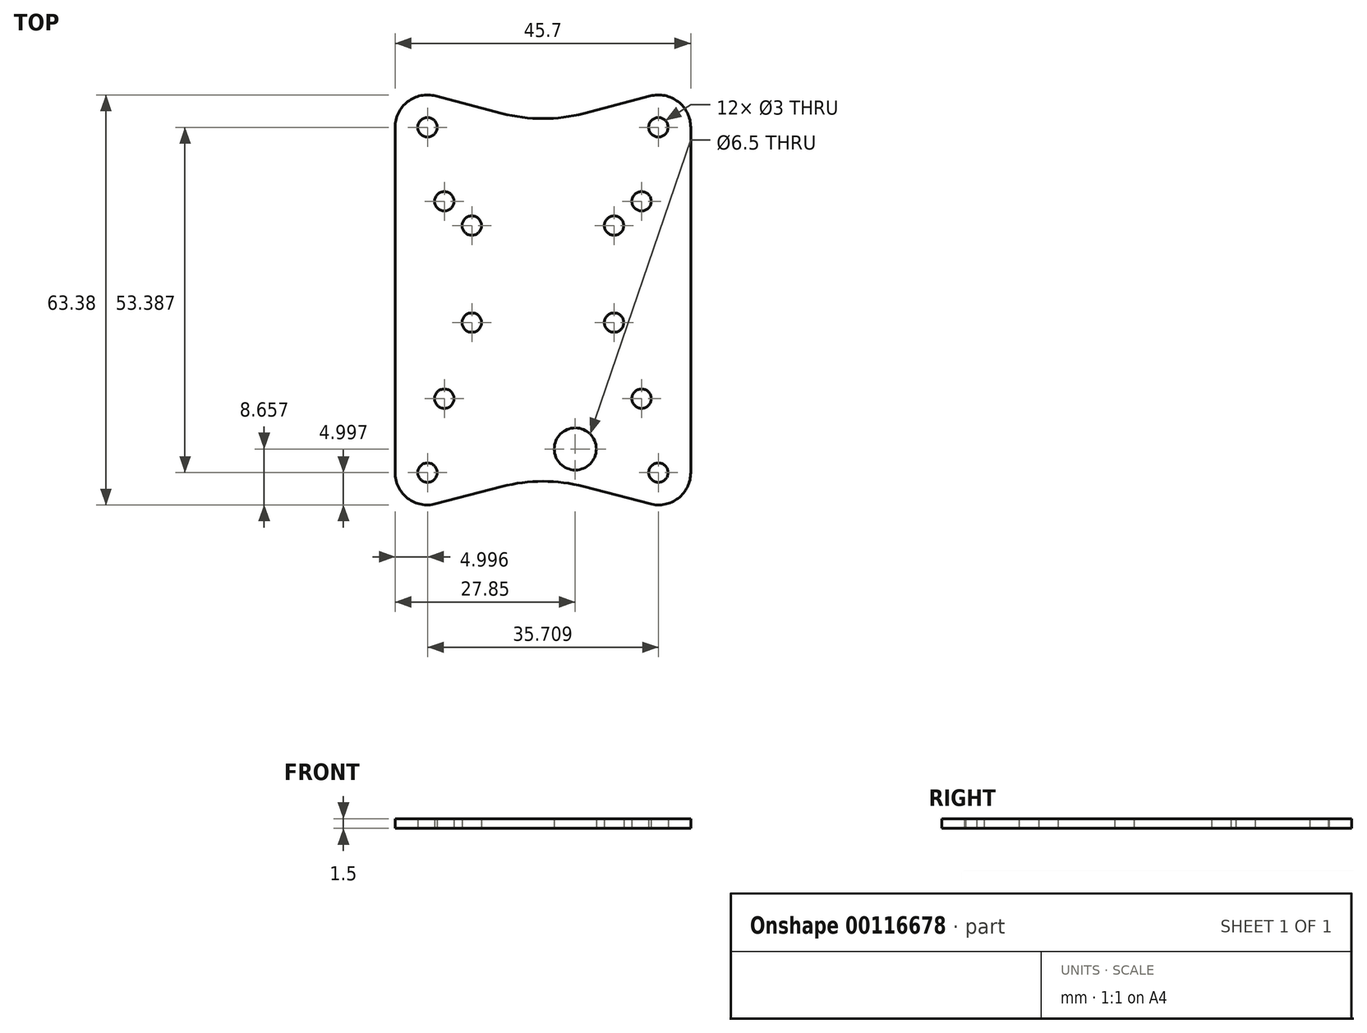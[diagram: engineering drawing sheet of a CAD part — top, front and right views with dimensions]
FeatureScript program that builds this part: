
annotation { "Feature Type Name" : "Feature", "Feature Type Description" : "" }
export const myFeature = defineFeature(function(context is Context, id is Id, definition is map)
    precondition{}
    {
        {
            var Q0;
            Q0=qCreatedBy(makeId("Top.planeOp"),FACE);
            var sketch = newSketch(context, id + "F0", { "sketchPlane" : qUnion([Q0])});
            skCircle(sketch, "E0", {"center": v(5, -23.03) * mm, "radius": 3.25 * mm});
            skArc(sketch, "E1", {"start": v(-6.33, 28.85) * mm, "mid": v(0, 28.03) * mm, "end": v(6.33, 28.85) * mm});
            skArc(sketch, "E2", {"start": v(6.33, -28.85) * mm, "mid": v(0, -28.03) * mm, "end": v(-6.33, -28.85) * mm});
            skCircle(sketch, "E3", {"center": v(-17.85, -26.7) * mm, "radius": 1.5 * mm});
            skCircle(sketch, "E4", {"center": v(17.85, -26.7) * mm, "radius": 1.5 * mm});
            skCircle(sketch, "E5", {"center": v(17.85, 26.7) * mm, "radius": 1.5 * mm});
            skCircle(sketch, "E6", {"center": v(-17.85, 26.7) * mm, "radius": 1.5 * mm});
            skArc(sketch, "E7", {"start": v(-16.59, 31.53) * mm, "mid": v(-20.91, 30.65) * mm, "end": v(-22.85, 26.7) * mm});
            skArc(sketch, "E8", {"start": v(22.85, 26.7) * mm, "mid": v(20.91, 30.65) * mm, "end": v(16.59, 31.53) * mm});
            skArc(sketch, "E9", {"start": v(-22.85, -26.7) * mm, "mid": v(-20.91, -30.65) * mm, "end": v(-16.59, -31.53) * mm});
            skArc(sketch, "E10", {"start": v(16.59, -31.53) * mm, "mid": v(20.91, -30.65) * mm, "end": v(22.85, -26.7) * mm});
            skLineSegment(sketch, "E11", {"start": v(-16.59, -31.53) * mm, "end": v(-6.33, -28.85) * mm});
            skLineSegment(sketch, "E12", {"start": v(6.33, -28.85) * mm, "end": v(16.59, -31.53) * mm});
            skLineSegment(sketch, "E13", {"start": v(22.85, -26.7) * mm, "end": v(22.85, 26.7) * mm});
            skLineSegment(sketch, "E14", {"start": v(-22.85, 26.7) * mm, "end": v(-22.85, -26.7) * mm});
            skLineSegment(sketch, "E15", {"start": v(-16.59, 31.53) * mm, "end": v(-6.33, 28.85) * mm});
            skLineSegment(sketch, "E16", {"start": v(16.59, 31.53) * mm, "end": v(6.33, 28.85) * mm});
            skCircle(sketch, "E17", {"center": v(-15.25, -15.25) * mm, "radius": 1.5 * mm});
            skCircle(sketch, "E18", {"center": v(15.25, -15.25) * mm, "radius": 1.5 * mm});
            skCircle(sketch, "E19", {"center": v(15.25, 15.25) * mm, "radius": 1.5 * mm});
            skCircle(sketch, "E20", {"center": v(-15.25, 15.25) * mm, "radius": 1.5 * mm});
            skCircle(sketch, "E21", {"center": v(-11, -3.5) * mm, "radius": 1.5 * mm});
            skCircle(sketch, "E22", {"center": v(-11, 11.5) * mm, "radius": 1.5 * mm});
            skCircle(sketch, "E23", {"center": v(11, -3.5) * mm, "radius": 1.5 * mm});
            skCircle(sketch, "E24", {"center": v(11, 11.5) * mm, "radius": 1.5 * mm});
            skSolve(sketch);
        }
        {
            var Q0;
            Q0 = qSketchRegion(id + "F0", true);
            extrude(context, id + "F1", {"entities" : qUnion([Q0]), "depth" : 1.5 * mm});
        }
    });
